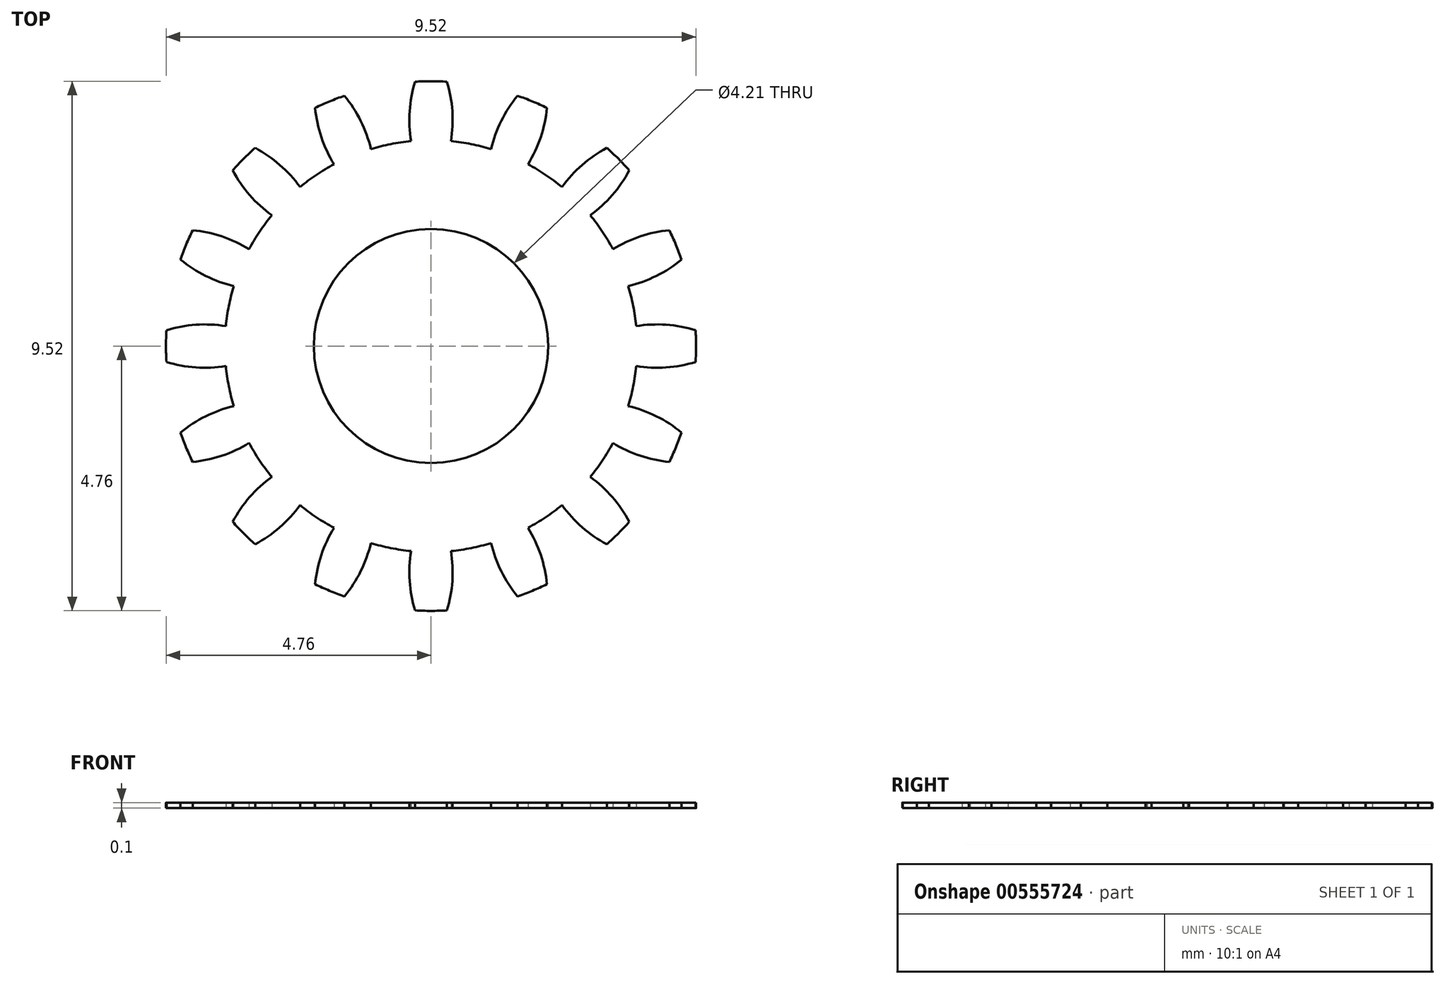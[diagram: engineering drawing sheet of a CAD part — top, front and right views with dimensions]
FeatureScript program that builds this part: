
annotation { "Feature Type Name" : "Feature", "Feature Type Description" : "" }
export const myFeature = defineFeature(function(context is Context, id is Id, definition is map)
    precondition{}
    {
        {
            var Q0;
            Q0=qCreatedBy(makeId("Top.planeOp"),FACE);
            var sketch = newSketch(context, id + "F0", { "sketchPlane" : qUnion([Q0])});
            skCircle(sketch, "E0", {"center": v(0, 0) * mm, "radius": 1.9 * mm});
            skCircle(sketch, "E1.0", {"center": v(0, 0) * mm, "radius": 2.1 * mm});
            skCircle(sketch, "E2", {"center": v(0, 0) * mm, "radius": 4.23 * mm});
            skLineSegment(sketch, "E3", {"start": v(0, 0) * mm, "end": v(0, 4.76) * mm});
            skLineSegment(sketch, "E4", {"start": v(0, 0) * mm, "end": v(0.93, 4.67) * mm});
            skCircle(sketch, "E5", {"center": v(0, 0) * mm, "radius": 4.76 * mm});
            skCircle(sketch, "E6", {"center": v(0, 0) * mm, "radius": 3.7 * mm});
            skPoint(sketch, "E7", {"position": v(0.38, 4.22) * mm});
            skPoint(sketch, "E8", {"position": v(0.29, 4.75) * mm});
            skPoint(sketch, "E9", {"position": v(0.36, 3.69) * mm});
            skArc(sketch, "E10", {"start": v(0.36, 3.69) * mm, "mid": v(0.38, 4.22) * mm, "end": v(0.29, 4.75) * mm});
            skArc(sketch, "E11", {"start": v(0.36, 3.69) * mm, "mid": v(0.54, 3.66) * mm, "end": v(0.72, 3.63) * mm});
            skArc(sketch, "E12", {"start": v(0, 4.76) * mm, "mid": v(0.14, 4.76) * mm, "end": v(0.29, 4.75) * mm});
            skPoint(sketch, "E13.MirrorP", {"position": v(-0.36, 3.69) * mm});
            skPoint(sketch, "E14.MirrorP", {"position": v(-0.29, 4.75) * mm});
            skArc(sketch, "E15.MirrorCS", {"start": v(-0.36, 3.69) * mm, "mid": v(-0.54, 3.66) * mm, "end": v(-0.72, 3.63) * mm});
            skArc(sketch, "E16.MirrorCS", {"start": v(0, 4.76) * mm, "mid": v(-0.14, 4.76) * mm, "end": v(-0.29, 4.75) * mm});
            skArc(sketch, "E17.MirrorCS", {"start": v(-0.36, 3.69) * mm, "mid": v(-0.38, 4.22) * mm, "end": v(-0.29, 4.75) * mm});
            skPoint(sketch, "E18.MirrorP", {"position": v(-0.38, 4.22) * mm});
            skPoint(sketch, "E19.1.0", {"position": v(-1.55, 4.5) * mm});
            skArc(sketch, "E19.1.1", {"start": v(-1.08, 3.54) * mm, "mid": v(-0.9, 3.6) * mm, "end": v(-0.72, 3.63) * mm});
            skArc(sketch, "E19.1.2", {"start": v(-1.74, 3.27) * mm, "mid": v(-1.9, 3.18) * mm, "end": v(-2.06, 3.08) * mm});
            skPoint(sketch, "E19.1.3", {"position": v(-2.08, 4.28) * mm});
            skPoint(sketch, "E19.1.4", {"position": v(-1.97, 3.75) * mm});
            skArc(sketch, "E19.1.5", {"start": v(-1.08, 3.54) * mm, "mid": v(-1.26, 4.05) * mm, "end": v(-1.55, 4.5) * mm});
            skPoint(sketch, "E19.1.6", {"position": v(-1.26, 4.04) * mm});
            skArc(sketch, "E19.1.7", {"start": v(-1.74, 3.27) * mm, "mid": v(-1.97, 3.76) * mm, "end": v(-2.08, 4.28) * mm});
            skPoint(sketch, "E19.1.8", {"position": v(-1.74, 3.27) * mm});
            skPoint(sketch, "E19.1.9", {"position": v(-1.08, 3.54) * mm});
            skArc(sketch, "E19.1.10", {"start": v(-1.82, 4.4) * mm, "mid": v(-1.69, 4.45) * mm, "end": v(-1.55, 4.5) * mm});
            skArc(sketch, "E19.1.11", {"start": v(-1.82, 4.4) * mm, "mid": v(-1.95, 4.34) * mm, "end": v(-2.08, 4.28) * mm});
            skPoint(sketch, "E19.2.0", {"position": v(-3.16, 3.56) * mm});
            skArc(sketch, "E19.2.1", {"start": v(-2.35, 2.86) * mm, "mid": v(-2.2, 2.97) * mm, "end": v(-2.06, 3.08) * mm});
            skArc(sketch, "E19.2.2", {"start": v(-2.86, 2.35) * mm, "mid": v(-2.97, 2.2) * mm, "end": v(-3.08, 2.06) * mm});
            skPoint(sketch, "E19.2.3", {"position": v(-3.56, 3.16) * mm});
            skPoint(sketch, "E19.2.4", {"position": v(-3.25, 2.7) * mm});
            skArc(sketch, "E19.2.5", {"start": v(-2.35, 2.86) * mm, "mid": v(-2.72, 3.26) * mm, "end": v(-3.16, 3.56) * mm});
            skPoint(sketch, "E19.2.6", {"position": v(-2.7, 3.25) * mm});
            skArc(sketch, "E19.2.7", {"start": v(-2.86, 2.35) * mm, "mid": v(-3.26, 2.72) * mm, "end": v(-3.56, 3.16) * mm});
            skPoint(sketch, "E19.2.8", {"position": v(-2.86, 2.35) * mm});
            skPoint(sketch, "E19.2.9", {"position": v(-2.35, 2.86) * mm});
            skArc(sketch, "E19.2.10", {"start": v(-3.37, 3.37) * mm, "mid": v(-3.26, 3.47) * mm, "end": v(-3.16, 3.56) * mm});
            skArc(sketch, "E19.2.11", {"start": v(-3.37, 3.37) * mm, "mid": v(-3.47, 3.26) * mm, "end": v(-3.56, 3.16) * mm});
            skPoint(sketch, "E19.3.0", {"position": v(-4.28, 2.08) * mm});
            skArc(sketch, "E19.3.1", {"start": v(-3.27, 1.74) * mm, "mid": v(-3.18, 1.9) * mm, "end": v(-3.08, 2.06) * mm});
            skArc(sketch, "E19.3.2", {"start": v(-3.54, 1.08) * mm, "mid": v(-3.6, 0.9) * mm, "end": v(-3.63, 0.72) * mm});
            skPoint(sketch, "E19.3.3", {"position": v(-4.5, 1.55) * mm});
            skPoint(sketch, "E19.3.4", {"position": v(-4.04, 1.26) * mm});
            skArc(sketch, "E19.3.5", {"start": v(-3.27, 1.74) * mm, "mid": v(-3.76, 1.97) * mm, "end": v(-4.28, 2.08) * mm});
            skPoint(sketch, "E19.3.6", {"position": v(-3.75, 1.97) * mm});
            skArc(sketch, "E19.3.7", {"start": v(-3.54, 1.08) * mm, "mid": v(-4.05, 1.26) * mm, "end": v(-4.5, 1.55) * mm});
            skPoint(sketch, "E19.3.8", {"position": v(-3.54, 1.08) * mm});
            skPoint(sketch, "E19.3.9", {"position": v(-3.27, 1.74) * mm});
            skArc(sketch, "E19.3.10", {"start": v(-4.4, 1.82) * mm, "mid": v(-4.34, 1.95) * mm, "end": v(-4.28, 2.08) * mm});
            skArc(sketch, "E19.3.11", {"start": v(-4.4, 1.82) * mm, "mid": v(-4.45, 1.69) * mm, "end": v(-4.5, 1.55) * mm});
            skPoint(sketch, "E19.4.0", {"position": v(-4.75, 0.29) * mm});
            skArc(sketch, "E19.4.1", {"start": v(-3.69, 0.36) * mm, "mid": v(-3.66, 0.54) * mm, "end": v(-3.63, 0.72) * mm});
            skArc(sketch, "E19.4.2", {"start": v(-3.69, -0.36) * mm, "mid": v(-3.66, -0.54) * mm, "end": v(-3.63, -0.72) * mm});
            skPoint(sketch, "E19.4.3", {"position": v(-4.75, -0.29) * mm});
            skPoint(sketch, "E19.4.4", {"position": v(-4.22, -0.38) * mm});
            skArc(sketch, "E19.4.5", {"start": v(-3.69, 0.36) * mm, "mid": v(-4.22, 0.38) * mm, "end": v(-4.75, 0.29) * mm});
            skPoint(sketch, "E19.4.6", {"position": v(-4.22, 0.38) * mm});
            skArc(sketch, "E19.4.7", {"start": v(-3.69, -0.36) * mm, "mid": v(-4.22, -0.38) * mm, "end": v(-4.75, -0.29) * mm});
            skPoint(sketch, "E19.4.8", {"position": v(-3.69, -0.36) * mm});
            skPoint(sketch, "E19.4.9", {"position": v(-3.69, 0.36) * mm});
            skArc(sketch, "E19.4.10", {"start": v(-4.76, 0) * mm, "mid": v(-4.76, 0.14) * mm, "end": v(-4.75, 0.29) * mm});
            skArc(sketch, "E19.4.11", {"start": v(-4.76, 0) * mm, "mid": v(-4.76, -0.14) * mm, "end": v(-4.75, -0.29) * mm});
            skPoint(sketch, "E19.5.0", {"position": v(-4.5, -1.55) * mm});
            skArc(sketch, "E19.5.1", {"start": v(-3.54, -1.08) * mm, "mid": v(-3.6, -0.9) * mm, "end": v(-3.63, -0.72) * mm});
            skArc(sketch, "E19.5.2", {"start": v(-3.27, -1.74) * mm, "mid": v(-3.18, -1.9) * mm, "end": v(-3.08, -2.06) * mm});
            skPoint(sketch, "E19.5.3", {"position": v(-4.28, -2.08) * mm});
            skPoint(sketch, "E19.5.4", {"position": v(-3.75, -1.97) * mm});
            skArc(sketch, "E19.5.5", {"start": v(-3.54, -1.08) * mm, "mid": v(-4.05, -1.26) * mm, "end": v(-4.5, -1.55) * mm});
            skPoint(sketch, "E19.5.6", {"position": v(-4.04, -1.26) * mm});
            skArc(sketch, "E19.5.7", {"start": v(-3.27, -1.74) * mm, "mid": v(-3.76, -1.97) * mm, "end": v(-4.28, -2.08) * mm});
            skPoint(sketch, "E19.5.8", {"position": v(-3.27, -1.74) * mm});
            skPoint(sketch, "E19.5.9", {"position": v(-3.54, -1.08) * mm});
            skArc(sketch, "E19.5.10", {"start": v(-4.4, -1.82) * mm, "mid": v(-4.45, -1.69) * mm, "end": v(-4.5, -1.55) * mm});
            skArc(sketch, "E19.5.11", {"start": v(-4.4, -1.82) * mm, "mid": v(-4.34, -1.95) * mm, "end": v(-4.28, -2.08) * mm});
            skPoint(sketch, "E19.6.0", {"position": v(-3.56, -3.16) * mm});
            skArc(sketch, "E19.6.1", {"start": v(-2.86, -2.35) * mm, "mid": v(-2.97, -2.2) * mm, "end": v(-3.08, -2.06) * mm});
            skArc(sketch, "E19.6.2", {"start": v(-2.35, -2.86) * mm, "mid": v(-2.2, -2.97) * mm, "end": v(-2.06, -3.08) * mm});
            skPoint(sketch, "E19.6.3", {"position": v(-3.16, -3.56) * mm});
            skPoint(sketch, "E19.6.4", {"position": v(-2.7, -3.25) * mm});
            skArc(sketch, "E19.6.5", {"start": v(-2.86, -2.35) * mm, "mid": v(-3.26, -2.72) * mm, "end": v(-3.56, -3.16) * mm});
            skPoint(sketch, "E19.6.6", {"position": v(-3.25, -2.7) * mm});
            skArc(sketch, "E19.6.7", {"start": v(-2.35, -2.86) * mm, "mid": v(-2.72, -3.26) * mm, "end": v(-3.16, -3.56) * mm});
            skPoint(sketch, "E19.6.8", {"position": v(-2.35, -2.86) * mm});
            skPoint(sketch, "E19.6.9", {"position": v(-2.86, -2.35) * mm});
            skArc(sketch, "E19.6.10", {"start": v(-3.37, -3.37) * mm, "mid": v(-3.47, -3.26) * mm, "end": v(-3.56, -3.16) * mm});
            skArc(sketch, "E19.6.11", {"start": v(-3.37, -3.37) * mm, "mid": v(-3.26, -3.47) * mm, "end": v(-3.16, -3.56) * mm});
            skPoint(sketch, "E19.7.0", {"position": v(-2.08, -4.28) * mm});
            skArc(sketch, "E19.7.1", {"start": v(-1.74, -3.27) * mm, "mid": v(-1.9, -3.18) * mm, "end": v(-2.06, -3.08) * mm});
            skArc(sketch, "E19.7.2", {"start": v(-1.08, -3.54) * mm, "mid": v(-0.9, -3.6) * mm, "end": v(-0.72, -3.63) * mm});
            skPoint(sketch, "E19.7.3", {"position": v(-1.55, -4.5) * mm});
            skPoint(sketch, "E19.7.4", {"position": v(-1.26, -4.04) * mm});
            skArc(sketch, "E19.7.5", {"start": v(-1.74, -3.27) * mm, "mid": v(-1.97, -3.76) * mm, "end": v(-2.08, -4.28) * mm});
            skPoint(sketch, "E19.7.6", {"position": v(-1.97, -3.75) * mm});
            skArc(sketch, "E19.7.7", {"start": v(-1.08, -3.54) * mm, "mid": v(-1.26, -4.05) * mm, "end": v(-1.55, -4.5) * mm});
            skPoint(sketch, "E19.7.8", {"position": v(-1.08, -3.54) * mm});
            skPoint(sketch, "E19.7.9", {"position": v(-1.74, -3.27) * mm});
            skArc(sketch, "E19.7.10", {"start": v(-1.82, -4.4) * mm, "mid": v(-1.95, -4.34) * mm, "end": v(-2.08, -4.28) * mm});
            skArc(sketch, "E19.7.11", {"start": v(-1.82, -4.4) * mm, "mid": v(-1.69, -4.45) * mm, "end": v(-1.55, -4.5) * mm});
            skPoint(sketch, "E19.8.0", {"position": v(-0.29, -4.75) * mm});
            skArc(sketch, "E19.8.1", {"start": v(-0.36, -3.69) * mm, "mid": v(-0.54, -3.66) * mm, "end": v(-0.72, -3.63) * mm});
            skArc(sketch, "E19.8.2", {"start": v(0.36, -3.69) * mm, "mid": v(0.54, -3.66) * mm, "end": v(0.72, -3.63) * mm});
            skPoint(sketch, "E19.8.3", {"position": v(0.29, -4.75) * mm});
            skPoint(sketch, "E19.8.4", {"position": v(0.38, -4.22) * mm});
            skArc(sketch, "E19.8.5", {"start": v(-0.36, -3.69) * mm, "mid": v(-0.38, -4.22) * mm, "end": v(-0.29, -4.75) * mm});
            skPoint(sketch, "E19.8.6", {"position": v(-0.38, -4.22) * mm});
            skArc(sketch, "E19.8.7", {"start": v(0.36, -3.69) * mm, "mid": v(0.38, -4.22) * mm, "end": v(0.29, -4.75) * mm});
            skPoint(sketch, "E19.8.8", {"position": v(0.36, -3.69) * mm});
            skPoint(sketch, "E19.8.9", {"position": v(-0.36, -3.69) * mm});
            skArc(sketch, "E19.8.10", {"start": v(0, -4.76) * mm, "mid": v(-0.14, -4.76) * mm, "end": v(-0.29, -4.75) * mm});
            skArc(sketch, "E19.8.11", {"start": v(0, -4.76) * mm, "mid": v(0.14, -4.76) * mm, "end": v(0.29, -4.75) * mm});
            skPoint(sketch, "E19.9.0", {"position": v(1.55, -4.5) * mm});
            skArc(sketch, "E19.9.1", {"start": v(1.08, -3.54) * mm, "mid": v(0.9, -3.6) * mm, "end": v(0.72, -3.63) * mm});
            skArc(sketch, "E19.9.2", {"start": v(1.74, -3.27) * mm, "mid": v(1.9, -3.18) * mm, "end": v(2.06, -3.08) * mm});
            skPoint(sketch, "E19.9.3", {"position": v(2.08, -4.28) * mm});
            skPoint(sketch, "E19.9.4", {"position": v(1.97, -3.75) * mm});
            skArc(sketch, "E19.9.5", {"start": v(1.08, -3.54) * mm, "mid": v(1.26, -4.05) * mm, "end": v(1.55, -4.5) * mm});
            skPoint(sketch, "E19.9.6", {"position": v(1.26, -4.04) * mm});
            skArc(sketch, "E19.9.7", {"start": v(1.74, -3.27) * mm, "mid": v(1.97, -3.76) * mm, "end": v(2.08, -4.28) * mm});
            skPoint(sketch, "E19.9.8", {"position": v(1.74, -3.27) * mm});
            skPoint(sketch, "E19.9.9", {"position": v(1.08, -3.54) * mm});
            skArc(sketch, "E19.9.10", {"start": v(1.82, -4.4) * mm, "mid": v(1.69, -4.45) * mm, "end": v(1.55, -4.5) * mm});
            skArc(sketch, "E19.9.11", {"start": v(1.82, -4.4) * mm, "mid": v(1.95, -4.34) * mm, "end": v(2.08, -4.28) * mm});
            skPoint(sketch, "E19.10.0", {"position": v(3.16, -3.56) * mm});
            skArc(sketch, "E19.10.1", {"start": v(2.35, -2.86) * mm, "mid": v(2.2, -2.97) * mm, "end": v(2.06, -3.08) * mm});
            skArc(sketch, "E19.10.2", {"start": v(2.86, -2.35) * mm, "mid": v(2.97, -2.2) * mm, "end": v(3.08, -2.06) * mm});
            skPoint(sketch, "E19.10.3", {"position": v(3.56, -3.16) * mm});
            skPoint(sketch, "E19.10.4", {"position": v(3.25, -2.7) * mm});
            skArc(sketch, "E19.10.5", {"start": v(2.35, -2.86) * mm, "mid": v(2.72, -3.26) * mm, "end": v(3.16, -3.56) * mm});
            skPoint(sketch, "E19.10.6", {"position": v(2.7, -3.25) * mm});
            skArc(sketch, "E19.10.7", {"start": v(2.86, -2.35) * mm, "mid": v(3.26, -2.72) * mm, "end": v(3.56, -3.16) * mm});
            skPoint(sketch, "E19.10.8", {"position": v(2.86, -2.35) * mm});
            skPoint(sketch, "E19.10.9", {"position": v(2.35, -2.86) * mm});
            skArc(sketch, "E19.10.10", {"start": v(3.37, -3.37) * mm, "mid": v(3.26, -3.47) * mm, "end": v(3.16, -3.56) * mm});
            skArc(sketch, "E19.10.11", {"start": v(3.37, -3.37) * mm, "mid": v(3.47, -3.26) * mm, "end": v(3.56, -3.16) * mm});
            skPoint(sketch, "E19.11.0", {"position": v(4.28, -2.08) * mm});
            skArc(sketch, "E19.11.1", {"start": v(3.27, -1.74) * mm, "mid": v(3.18, -1.9) * mm, "end": v(3.08, -2.06) * mm});
            skArc(sketch, "E19.11.2", {"start": v(3.54, -1.08) * mm, "mid": v(3.6, -0.9) * mm, "end": v(3.63, -0.72) * mm});
            skPoint(sketch, "E19.11.3", {"position": v(4.5, -1.55) * mm});
            skPoint(sketch, "E19.11.4", {"position": v(4.04, -1.26) * mm});
            skArc(sketch, "E19.11.5", {"start": v(3.27, -1.74) * mm, "mid": v(3.76, -1.97) * mm, "end": v(4.28, -2.08) * mm});
            skPoint(sketch, "E19.11.6", {"position": v(3.75, -1.97) * mm});
            skArc(sketch, "E19.11.7", {"start": v(3.54, -1.08) * mm, "mid": v(4.05, -1.26) * mm, "end": v(4.5, -1.55) * mm});
            skPoint(sketch, "E19.11.8", {"position": v(3.54, -1.08) * mm});
            skPoint(sketch, "E19.11.9", {"position": v(3.27, -1.74) * mm});
            skArc(sketch, "E19.11.10", {"start": v(4.4, -1.82) * mm, "mid": v(4.34, -1.95) * mm, "end": v(4.28, -2.08) * mm});
            skArc(sketch, "E19.11.11", {"start": v(4.4, -1.82) * mm, "mid": v(4.45, -1.69) * mm, "end": v(4.5, -1.55) * mm});
            skPoint(sketch, "E19.12.0", {"position": v(4.75, -0.29) * mm});
            skArc(sketch, "E19.12.1", {"start": v(3.69, -0.36) * mm, "mid": v(3.66, -0.54) * mm, "end": v(3.63, -0.72) * mm});
            skArc(sketch, "E19.12.2", {"start": v(3.69, 0.36) * mm, "mid": v(3.66, 0.54) * mm, "end": v(3.63, 0.72) * mm});
            skPoint(sketch, "E19.12.3", {"position": v(4.75, 0.29) * mm});
            skPoint(sketch, "E19.12.4", {"position": v(4.22, 0.38) * mm});
            skArc(sketch, "E19.12.5", {"start": v(3.69, -0.36) * mm, "mid": v(4.22, -0.38) * mm, "end": v(4.75, -0.29) * mm});
            skPoint(sketch, "E19.12.6", {"position": v(4.22, -0.38) * mm});
            skArc(sketch, "E19.12.7", {"start": v(3.69, 0.36) * mm, "mid": v(4.22, 0.38) * mm, "end": v(4.75, 0.29) * mm});
            skPoint(sketch, "E19.12.8", {"position": v(3.69, 0.36) * mm});
            skPoint(sketch, "E19.12.9", {"position": v(3.69, -0.36) * mm});
            skArc(sketch, "E19.12.10", {"start": v(4.76, 0) * mm, "mid": v(4.76, -0.14) * mm, "end": v(4.75, -0.29) * mm});
            skArc(sketch, "E19.12.11", {"start": v(4.76, 0) * mm, "mid": v(4.76, 0.14) * mm, "end": v(4.75, 0.29) * mm});
            skPoint(sketch, "E19.13.0", {"position": v(4.5, 1.55) * mm});
            skArc(sketch, "E19.13.1", {"start": v(3.54, 1.08) * mm, "mid": v(3.6, 0.9) * mm, "end": v(3.63, 0.72) * mm});
            skArc(sketch, "E19.13.2", {"start": v(3.27, 1.74) * mm, "mid": v(3.18, 1.9) * mm, "end": v(3.08, 2.06) * mm});
            skPoint(sketch, "E19.13.3", {"position": v(4.28, 2.08) * mm});
            skPoint(sketch, "E19.13.4", {"position": v(3.75, 1.97) * mm});
            skArc(sketch, "E19.13.5", {"start": v(3.54, 1.08) * mm, "mid": v(4.05, 1.26) * mm, "end": v(4.5, 1.55) * mm});
            skPoint(sketch, "E19.13.6", {"position": v(4.04, 1.26) * mm});
            skArc(sketch, "E19.13.7", {"start": v(3.27, 1.74) * mm, "mid": v(3.76, 1.97) * mm, "end": v(4.28, 2.08) * mm});
            skPoint(sketch, "E19.13.8", {"position": v(3.27, 1.74) * mm});
            skPoint(sketch, "E19.13.9", {"position": v(3.54, 1.08) * mm});
            skArc(sketch, "E19.13.10", {"start": v(4.4, 1.82) * mm, "mid": v(4.45, 1.69) * mm, "end": v(4.5, 1.55) * mm});
            skArc(sketch, "E19.13.11", {"start": v(4.4, 1.82) * mm, "mid": v(4.34, 1.95) * mm, "end": v(4.28, 2.08) * mm});
            skPoint(sketch, "E19.14.0", {"position": v(3.56, 3.16) * mm});
            skArc(sketch, "E19.14.1", {"start": v(2.86, 2.35) * mm, "mid": v(2.97, 2.2) * mm, "end": v(3.08, 2.06) * mm});
            skArc(sketch, "E19.14.2", {"start": v(2.35, 2.86) * mm, "mid": v(2.2, 2.97) * mm, "end": v(2.06, 3.08) * mm});
            skPoint(sketch, "E19.14.3", {"position": v(3.16, 3.56) * mm});
            skPoint(sketch, "E19.14.4", {"position": v(2.7, 3.25) * mm});
            skArc(sketch, "E19.14.5", {"start": v(2.86, 2.35) * mm, "mid": v(3.26, 2.72) * mm, "end": v(3.56, 3.16) * mm});
            skPoint(sketch, "E19.14.6", {"position": v(3.25, 2.7) * mm});
            skArc(sketch, "E19.14.7", {"start": v(2.35, 2.86) * mm, "mid": v(2.72, 3.26) * mm, "end": v(3.16, 3.56) * mm});
            skPoint(sketch, "E19.14.8", {"position": v(2.35, 2.86) * mm});
            skPoint(sketch, "E19.14.9", {"position": v(2.86, 2.35) * mm});
            skArc(sketch, "E19.14.10", {"start": v(3.37, 3.37) * mm, "mid": v(3.47, 3.26) * mm, "end": v(3.56, 3.16) * mm});
            skArc(sketch, "E19.14.11", {"start": v(3.37, 3.37) * mm, "mid": v(3.26, 3.47) * mm, "end": v(3.16, 3.56) * mm});
            skPoint(sketch, "E19.15.0", {"position": v(2.08, 4.28) * mm});
            skArc(sketch, "E19.15.1", {"start": v(1.74, 3.27) * mm, "mid": v(1.9, 3.18) * mm, "end": v(2.06, 3.08) * mm});
            skArc(sketch, "E19.15.2", {"start": v(1.08, 3.54) * mm, "mid": v(0.9, 3.6) * mm, "end": v(0.72, 3.63) * mm});
            skPoint(sketch, "E19.15.3", {"position": v(1.55, 4.5) * mm});
            skPoint(sketch, "E19.15.4", {"position": v(1.26, 4.04) * mm});
            skArc(sketch, "E19.15.5", {"start": v(1.74, 3.27) * mm, "mid": v(1.97, 3.76) * mm, "end": v(2.08, 4.28) * mm});
            skPoint(sketch, "E19.15.6", {"position": v(1.97, 3.75) * mm});
            skArc(sketch, "E19.15.7", {"start": v(1.08, 3.54) * mm, "mid": v(1.26, 4.05) * mm, "end": v(1.55, 4.5) * mm});
            skPoint(sketch, "E19.15.8", {"position": v(1.08, 3.54) * mm});
            skPoint(sketch, "E19.15.9", {"position": v(1.74, 3.27) * mm});
            skArc(sketch, "E19.15.10", {"start": v(1.82, 4.4) * mm, "mid": v(1.95, 4.34) * mm, "end": v(2.08, 4.28) * mm});
            skArc(sketch, "E19.15.11", {"start": v(1.82, 4.4) * mm, "mid": v(1.69, 4.45) * mm, "end": v(1.55, 4.5) * mm});
            skSolve(sketch);
        }
        {
            var Q0;
            {var subQ0=sQuery(id+"F0.wireOp",EDGE,"E19.13.5");var subQ1=sQuery(id+"F0.wireOp",EDGE,"E2");var subQ2=makeQuery(id+"F0.imprint","INTERSECT",VERTEX,{"derivedFrom":[subQ1,subQ0]});Q0=makeQuery(id+"F0.imprint","IMPRINT",FACE,{"disambiguationData":[TD([[makeQuery(id+"F0.imprint","IMPRINT",EDGE,{"disambiguationData":[TD([[subQ2,-1.0]])],"derivedFrom":subQ1}),-1.0]])]});}
            var Q1;
            {var subQ0=sQuery(id+"F0.wireOp",EDGE,"E19.14.5");var subQ1=sQuery(id+"F0.wireOp",EDGE,"E2");var subQ2=makeQuery(id+"F0.imprint","INTERSECT",VERTEX,{"derivedFrom":[subQ1,subQ0]});Q1=makeQuery(id+"F0.imprint","IMPRINT",FACE,{"disambiguationData":[TD([[makeQuery(id+"F0.imprint","IMPRINT",EDGE,{"disambiguationData":[TD([[subQ2,-1.0]])],"derivedFrom":subQ1}),-1.0]])]});}
            var Q2;
            {var subQ0=sQuery(id+"F0.wireOp",EDGE,"E19.15.5");var subQ1=sQuery(id+"F0.wireOp",EDGE,"E2");var subQ2=makeQuery(id+"F0.imprint","INTERSECT",VERTEX,{"derivedFrom":[subQ1,subQ0]});Q2=makeQuery(id+"F0.imprint","IMPRINT",FACE,{"disambiguationData":[TD([[makeQuery(id+"F0.imprint","IMPRINT",EDGE,{"disambiguationData":[TD([[subQ2,-1.0]])],"derivedFrom":subQ1}),-1.0]])]});}
            var Q3;
            {var subQ0=sQuery(id+"F0.wireOp",EDGE,"E10");var subQ1=sQuery(id+"F0.wireOp",EDGE,"E2");var subQ2=makeQuery(id+"F0.imprint","INTERSECT",VERTEX,{"derivedFrom":[subQ1,subQ0]});Q3=makeQuery(id+"F0.imprint","IMPRINT",FACE,{"disambiguationData":[TD([[makeQuery(id+"F0.imprint","IMPRINT",EDGE,{"disambiguationData":[TD([[subQ2,-1.0]])],"derivedFrom":subQ1}),-1.0]])]});}
            var Q4;
            {var subQ0=sQuery(id+"F0.wireOp",EDGE,"E3");var subQ1=sQuery(id+"F0.wireOp",EDGE,"E2");var subQ2=makeQuery(id+"F0.imprint","INTERSECT",VERTEX,{"derivedFrom":[subQ1,subQ0]});Q4=makeQuery(id+"F0.imprint","IMPRINT",FACE,{"disambiguationData":[TD([[makeQuery(id+"F0.imprint","IMPRINT",EDGE,{"disambiguationData":[TD([[subQ2,-1.0]])],"derivedFrom":subQ1}),-1.0]])]});}
            var Q5;
            {var subQ0=sQuery(id+"F0.wireOp",EDGE,"E19.1.5");var subQ1=sQuery(id+"F0.wireOp",EDGE,"E2");var subQ2=makeQuery(id+"F0.imprint","INTERSECT",VERTEX,{"derivedFrom":[subQ1,subQ0]});Q5=makeQuery(id+"F0.imprint","IMPRINT",FACE,{"disambiguationData":[TD([[makeQuery(id+"F0.imprint","IMPRINT",EDGE,{"disambiguationData":[TD([[subQ2,-1.0]])],"derivedFrom":subQ1}),-1.0]])]});}
            var Q6;
            {var subQ0=sQuery(id+"F0.wireOp",EDGE,"E19.2.5");var subQ1=sQuery(id+"F0.wireOp",EDGE,"E2");var subQ2=makeQuery(id+"F0.imprint","INTERSECT",VERTEX,{"derivedFrom":[subQ1,subQ0]});Q6=makeQuery(id+"F0.imprint","IMPRINT",FACE,{"disambiguationData":[TD([[makeQuery(id+"F0.imprint","IMPRINT",EDGE,{"disambiguationData":[TD([[subQ2,-1.0]])],"derivedFrom":subQ1}),-1.0]])]});}
            var Q7;
            {var subQ0=sQuery(id+"F0.wireOp",EDGE,"E19.3.5");var subQ1=sQuery(id+"F0.wireOp",EDGE,"E2");var subQ2=makeQuery(id+"F0.imprint","INTERSECT",VERTEX,{"derivedFrom":[subQ1,subQ0]});Q7=makeQuery(id+"F0.imprint","IMPRINT",FACE,{"disambiguationData":[TD([[makeQuery(id+"F0.imprint","IMPRINT",EDGE,{"disambiguationData":[TD([[subQ2,-1.0]])],"derivedFrom":subQ1}),-1.0]])]});}
            var Q8;
            {var subQ0=sQuery(id+"F0.wireOp",EDGE,"E19.4.5");var subQ1=sQuery(id+"F0.wireOp",EDGE,"E2");var subQ2=makeQuery(id+"F0.imprint","INTERSECT",VERTEX,{"derivedFrom":[subQ1,subQ0]});Q8=makeQuery(id+"F0.imprint","IMPRINT",FACE,{"disambiguationData":[TD([[makeQuery(id+"F0.imprint","IMPRINT",EDGE,{"disambiguationData":[TD([[subQ2,-1.0]])],"derivedFrom":subQ1}),-1.0]])]});}
            var Q9;
            {var subQ0=sQuery(id+"F0.wireOp",EDGE,"E19.5.5");var subQ1=sQuery(id+"F0.wireOp",EDGE,"E2");var subQ2=makeQuery(id+"F0.imprint","INTERSECT",VERTEX,{"derivedFrom":[subQ1,subQ0]});Q9=makeQuery(id+"F0.imprint","IMPRINT",FACE,{"disambiguationData":[TD([[makeQuery(id+"F0.imprint","IMPRINT",EDGE,{"disambiguationData":[TD([[subQ2,-1.0]])],"derivedFrom":subQ1}),-1.0]])]});}
            var Q10;
            {var subQ0=sQuery(id+"F0.wireOp",EDGE,"E19.6.5");var subQ1=sQuery(id+"F0.wireOp",EDGE,"E2");var subQ2=makeQuery(id+"F0.imprint","INTERSECT",VERTEX,{"derivedFrom":[subQ1,subQ0]});Q10=makeQuery(id+"F0.imprint","IMPRINT",FACE,{"disambiguationData":[TD([[makeQuery(id+"F0.imprint","IMPRINT",EDGE,{"disambiguationData":[TD([[subQ2,-1.0]])],"derivedFrom":subQ1}),-1.0]])]});}
            var Q11;
            {var subQ0=sQuery(id+"F0.wireOp",EDGE,"E19.7.5");var subQ1=sQuery(id+"F0.wireOp",EDGE,"E2");var subQ2=makeQuery(id+"F0.imprint","INTERSECT",VERTEX,{"derivedFrom":[subQ1,subQ0]});Q11=makeQuery(id+"F0.imprint","IMPRINT",FACE,{"disambiguationData":[TD([[makeQuery(id+"F0.imprint","IMPRINT",EDGE,{"disambiguationData":[TD([[subQ2,-1.0]])],"derivedFrom":subQ1}),-1.0]])]});}
            var Q12;
            {var subQ0=sQuery(id+"F0.wireOp",EDGE,"E19.8.5");var subQ1=sQuery(id+"F0.wireOp",EDGE,"E2");var subQ2=makeQuery(id+"F0.imprint","INTERSECT",VERTEX,{"derivedFrom":[subQ1,subQ0]});Q12=makeQuery(id+"F0.imprint","IMPRINT",FACE,{"disambiguationData":[TD([[makeQuery(id+"F0.imprint","IMPRINT",EDGE,{"disambiguationData":[TD([[subQ2,-1.0]])],"derivedFrom":subQ1}),-1.0]])]});}
            var Q13;
            {var subQ0=sQuery(id+"F0.wireOp",EDGE,"E19.9.5");var subQ1=sQuery(id+"F0.wireOp",EDGE,"E2");var subQ2=makeQuery(id+"F0.imprint","INTERSECT",VERTEX,{"derivedFrom":[subQ1,subQ0]});Q13=makeQuery(id+"F0.imprint","IMPRINT",FACE,{"disambiguationData":[TD([[makeQuery(id+"F0.imprint","IMPRINT",EDGE,{"disambiguationData":[TD([[subQ2,-1.0]])],"derivedFrom":subQ1}),-1.0]])]});}
            var Q14;
            {var subQ0=sQuery(id+"F0.wireOp",EDGE,"E19.10.5");var subQ1=sQuery(id+"F0.wireOp",EDGE,"E2");var subQ2=makeQuery(id+"F0.imprint","INTERSECT",VERTEX,{"derivedFrom":[subQ1,subQ0]});Q14=makeQuery(id+"F0.imprint","IMPRINT",FACE,{"disambiguationData":[TD([[makeQuery(id+"F0.imprint","IMPRINT",EDGE,{"disambiguationData":[TD([[subQ2,-1.0]])],"derivedFrom":subQ1}),-1.0]])]});}
            var Q15;
            {var subQ0=sQuery(id+"F0.wireOp",EDGE,"E19.11.5");var subQ1=sQuery(id+"F0.wireOp",EDGE,"E2");var subQ2=makeQuery(id+"F0.imprint","INTERSECT",VERTEX,{"derivedFrom":[subQ1,subQ0]});Q15=makeQuery(id+"F0.imprint","IMPRINT",FACE,{"disambiguationData":[TD([[makeQuery(id+"F0.imprint","IMPRINT",EDGE,{"disambiguationData":[TD([[subQ2,-1.0]])],"derivedFrom":subQ1}),-1.0]])]});}
            var Q16;
            {var subQ0=sQuery(id+"F0.wireOp",EDGE,"E19.12.7");var subQ1=sQuery(id+"F0.wireOp",EDGE,"E2");var subQ2=makeQuery(id+"F0.imprint","INTERSECT",VERTEX,{"derivedFrom":[subQ1,subQ0]});Q16=makeQuery(id+"F0.imprint","IMPRINT",FACE,{"disambiguationData":[TD([[makeQuery(id+"F0.imprint","IMPRINT",EDGE,{"disambiguationData":[TD([[subQ2,1.0]])],"derivedFrom":subQ1}),-1.0]])]});}
            var Q17;
            {var subQ0=sQuery(id+"F0.wireOp",EDGE,"E19.3.5");var subQ1=sQuery(id+"F0.wireOp",EDGE,"E2");var subQ2=makeQuery(id+"F0.imprint","INTERSECT",VERTEX,{"derivedFrom":[subQ1,subQ0]});Q17=makeQuery(id+"F0.imprint","IMPRINT",FACE,{"disambiguationData":[TD([[makeQuery(id+"F0.imprint","IMPRINT",EDGE,{"disambiguationData":[TD([[subQ2,-1.0]])],"derivedFrom":subQ1}),1.0]])]});}
            var Q18;
            {var subQ0=sQuery(id+"F0.wireOp",EDGE,"E19.4.5");var subQ1=sQuery(id+"F0.wireOp",EDGE,"E2");var subQ2=makeQuery(id+"F0.imprint","INTERSECT",VERTEX,{"derivedFrom":[subQ1,subQ0]});Q18=makeQuery(id+"F0.imprint","IMPRINT",FACE,{"disambiguationData":[TD([[makeQuery(id+"F0.imprint","IMPRINT",EDGE,{"disambiguationData":[TD([[subQ2,-1.0]])],"derivedFrom":subQ1}),1.0]])]});}
            var Q19;
            {var subQ0=sQuery(id+"F0.wireOp",EDGE,"E19.5.5");var subQ1=sQuery(id+"F0.wireOp",EDGE,"E2");var subQ2=makeQuery(id+"F0.imprint","INTERSECT",VERTEX,{"derivedFrom":[subQ1,subQ0]});Q19=makeQuery(id+"F0.imprint","IMPRINT",FACE,{"disambiguationData":[TD([[makeQuery(id+"F0.imprint","IMPRINT",EDGE,{"disambiguationData":[TD([[subQ2,-1.0]])],"derivedFrom":subQ1}),1.0]])]});}
            var Q20;
            {var subQ0=sQuery(id+"F0.wireOp",EDGE,"E19.6.5");var subQ1=sQuery(id+"F0.wireOp",EDGE,"E2");var subQ2=makeQuery(id+"F0.imprint","INTERSECT",VERTEX,{"derivedFrom":[subQ1,subQ0]});Q20=makeQuery(id+"F0.imprint","IMPRINT",FACE,{"disambiguationData":[TD([[makeQuery(id+"F0.imprint","IMPRINT",EDGE,{"disambiguationData":[TD([[subQ2,-1.0]])],"derivedFrom":subQ1}),1.0]])]});}
            var Q21;
            {var subQ0=sQuery(id+"F0.wireOp",EDGE,"E19.7.5");var subQ1=sQuery(id+"F0.wireOp",EDGE,"E2");var subQ2=makeQuery(id+"F0.imprint","INTERSECT",VERTEX,{"derivedFrom":[subQ1,subQ0]});Q21=makeQuery(id+"F0.imprint","IMPRINT",FACE,{"disambiguationData":[TD([[makeQuery(id+"F0.imprint","IMPRINT",EDGE,{"disambiguationData":[TD([[subQ2,-1.0]])],"derivedFrom":subQ1}),1.0]])]});}
            var Q22;
            {var subQ0=sQuery(id+"F0.wireOp",EDGE,"E19.8.5");var subQ1=sQuery(id+"F0.wireOp",EDGE,"E2");var subQ2=makeQuery(id+"F0.imprint","INTERSECT",VERTEX,{"derivedFrom":[subQ1,subQ0]});Q22=makeQuery(id+"F0.imprint","IMPRINT",FACE,{"disambiguationData":[TD([[makeQuery(id+"F0.imprint","IMPRINT",EDGE,{"disambiguationData":[TD([[subQ2,-1.0]])],"derivedFrom":subQ1}),1.0]])]});}
            var Q23;
            {var subQ0=sQuery(id+"F0.wireOp",EDGE,"E19.9.5");var subQ1=sQuery(id+"F0.wireOp",EDGE,"E2");var subQ2=makeQuery(id+"F0.imprint","INTERSECT",VERTEX,{"derivedFrom":[subQ1,subQ0]});Q23=makeQuery(id+"F0.imprint","IMPRINT",FACE,{"disambiguationData":[TD([[makeQuery(id+"F0.imprint","IMPRINT",EDGE,{"disambiguationData":[TD([[subQ2,-1.0]])],"derivedFrom":subQ1}),1.0]])]});}
            var Q24;
            {var subQ0=sQuery(id+"F0.wireOp",EDGE,"E19.10.5");var subQ1=sQuery(id+"F0.wireOp",EDGE,"E2");var subQ2=makeQuery(id+"F0.imprint","INTERSECT",VERTEX,{"derivedFrom":[subQ1,subQ0]});Q24=makeQuery(id+"F0.imprint","IMPRINT",FACE,{"disambiguationData":[TD([[makeQuery(id+"F0.imprint","IMPRINT",EDGE,{"disambiguationData":[TD([[subQ2,-1.0]])],"derivedFrom":subQ1}),1.0]])]});}
            var Q25;
            {var subQ0=sQuery(id+"F0.wireOp",EDGE,"E19.11.5");var subQ1=sQuery(id+"F0.wireOp",EDGE,"E2");var subQ2=makeQuery(id+"F0.imprint","INTERSECT",VERTEX,{"derivedFrom":[subQ1,subQ0]});Q25=makeQuery(id+"F0.imprint","IMPRINT",FACE,{"disambiguationData":[TD([[makeQuery(id+"F0.imprint","IMPRINT",EDGE,{"disambiguationData":[TD([[subQ2,-1.0]])],"derivedFrom":subQ1}),1.0]])]});}
            var Q26;
            {var subQ0=sQuery(id+"F0.wireOp",EDGE,"E19.12.7");var subQ1=sQuery(id+"F0.wireOp",EDGE,"E2");var subQ2=makeQuery(id+"F0.imprint","INTERSECT",VERTEX,{"derivedFrom":[subQ1,subQ0]});Q26=makeQuery(id+"F0.imprint","IMPRINT",FACE,{"disambiguationData":[TD([[makeQuery(id+"F0.imprint","IMPRINT",EDGE,{"disambiguationData":[TD([[subQ2,1.0]])],"derivedFrom":subQ1}),1.0]])]});}
            var Q27;
            {var subQ0=sQuery(id+"F0.wireOp",EDGE,"E19.13.5");var subQ1=sQuery(id+"F0.wireOp",EDGE,"E2");var subQ2=makeQuery(id+"F0.imprint","INTERSECT",VERTEX,{"derivedFrom":[subQ1,subQ0]});Q27=makeQuery(id+"F0.imprint","IMPRINT",FACE,{"disambiguationData":[TD([[makeQuery(id+"F0.imprint","IMPRINT",EDGE,{"disambiguationData":[TD([[subQ2,-1.0]])],"derivedFrom":subQ1}),1.0]])]});}
            var Q28;
            {var subQ0=sQuery(id+"F0.wireOp",EDGE,"E19.14.5");var subQ1=sQuery(id+"F0.wireOp",EDGE,"E2");var subQ2=makeQuery(id+"F0.imprint","INTERSECT",VERTEX,{"derivedFrom":[subQ1,subQ0]});Q28=makeQuery(id+"F0.imprint","IMPRINT",FACE,{"disambiguationData":[TD([[makeQuery(id+"F0.imprint","IMPRINT",EDGE,{"disambiguationData":[TD([[subQ2,-1.0]])],"derivedFrom":subQ1}),1.0]])]});}
            var Q29;
            {var subQ0=sQuery(id+"F0.wireOp",EDGE,"E19.15.5");var subQ1=sQuery(id+"F0.wireOp",EDGE,"E2");var subQ2=makeQuery(id+"F0.imprint","INTERSECT",VERTEX,{"derivedFrom":[subQ1,subQ0]});Q29=makeQuery(id+"F0.imprint","IMPRINT",FACE,{"disambiguationData":[TD([[makeQuery(id+"F0.imprint","IMPRINT",EDGE,{"disambiguationData":[TD([[subQ2,-1.0]])],"derivedFrom":subQ1}),1.0]])]});}
            var Q30;
            {var subQ0=sQuery(id+"F0.wireOp",EDGE,"E10");var subQ1=sQuery(id+"F0.wireOp",EDGE,"E2");var subQ2=makeQuery(id+"F0.imprint","INTERSECT",VERTEX,{"derivedFrom":[subQ1,subQ0]});Q30=makeQuery(id+"F0.imprint","IMPRINT",FACE,{"disambiguationData":[TD([[makeQuery(id+"F0.imprint","IMPRINT",EDGE,{"disambiguationData":[TD([[subQ2,-1.0]])],"derivedFrom":subQ1}),1.0]])]});}
            var Q31;
            {var subQ0=sQuery(id+"F0.wireOp",EDGE,"E3");var subQ1=sQuery(id+"F0.wireOp",EDGE,"E2");var subQ2=makeQuery(id+"F0.imprint","INTERSECT",VERTEX,{"derivedFrom":[subQ1,subQ0]});Q31=makeQuery(id+"F0.imprint","IMPRINT",FACE,{"disambiguationData":[TD([[makeQuery(id+"F0.imprint","IMPRINT",EDGE,{"disambiguationData":[TD([[subQ2,-1.0]])],"derivedFrom":subQ1}),1.0]])]});}
            var Q32;
            {var subQ0=sQuery(id+"F0.wireOp",EDGE,"E19.1.5");var subQ1=sQuery(id+"F0.wireOp",EDGE,"E2");var subQ2=makeQuery(id+"F0.imprint","INTERSECT",VERTEX,{"derivedFrom":[subQ1,subQ0]});Q32=makeQuery(id+"F0.imprint","IMPRINT",FACE,{"disambiguationData":[TD([[makeQuery(id+"F0.imprint","IMPRINT",EDGE,{"disambiguationData":[TD([[subQ2,-1.0]])],"derivedFrom":subQ1}),1.0]])]});}
            var Q33;
            {var subQ0=sQuery(id+"F0.wireOp",EDGE,"E19.2.5");var subQ1=sQuery(id+"F0.wireOp",EDGE,"E2");var subQ2=makeQuery(id+"F0.imprint","INTERSECT",VERTEX,{"derivedFrom":[subQ1,subQ0]});Q33=makeQuery(id+"F0.imprint","IMPRINT",FACE,{"disambiguationData":[TD([[makeQuery(id+"F0.imprint","IMPRINT",EDGE,{"disambiguationData":[TD([[subQ2,-1.0]])],"derivedFrom":subQ1}),1.0]])]});}
            var Q34;
            {var subQ9=sQuery(id+"F0.wireOp",EDGE,"E3");var subQ10=sQuery(id+"F0.wireOp",EDGE,"E1.0");var subQ11=makeQuery(id+"F0.imprint","INTERSECT",VERTEX,{"derivedFrom":[subQ10,subQ9]});Q34=makeQuery(id+"F0.imprint","IMPRINT",FACE,{"disambiguationData":[TD([[makeQuery(id+"F0.imprint","IMPRINT",EDGE,{"disambiguationData":[TD([[subQ11,-1.0]])],"derivedFrom":subQ10}),-1.0]])]});}
            var Q35;
            {var subQ4=sQuery(id+"F0.wireOp",EDGE,"E3");var subQ5=sQuery(id+"F0.wireOp",EDGE,"E1.0");var subQ6=makeQuery(id+"F0.imprint","INTERSECT",VERTEX,{"derivedFrom":[subQ5,subQ4]});Q35=makeQuery(id+"F0.imprint","IMPRINT",FACE,{"disambiguationData":[TD([[makeQuery(id+"F0.imprint","IMPRINT",EDGE,{"disambiguationData":[TD([[subQ6,1.0]])],"derivedFrom":subQ5}),-1.0]])]});}
            extrude(context, id + "F1", {"entities" : qUnion([Q0, Q1, Q2, Q3, Q4, Q5, Q6, Q7, Q8, Q9, Q10, Q11, Q12, Q13, Q14, Q15, Q16, Q17, Q18, Q19, Q20, Q21, Q22, Q23, Q24, Q25, Q26, Q27, Q28, Q29, Q30, Q31, Q32, Q33, Q34, Q35]), "depth" : .1 * mm, "offsetDistance" : 25.4 * mm});
        }
    });
